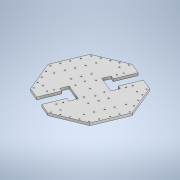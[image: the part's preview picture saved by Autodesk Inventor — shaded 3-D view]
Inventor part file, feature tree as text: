
AUTODESK INVENTOR PART (.ipt)
format: ipt  version: 2020 (Build 240168000, 168)  size: 396,288 bytes
history: native  units: mm
features: extrude x2, sketch x2
ambient origin geometry x8: Origin, YZ Plane, XZ Plane, XY Plane, X Axis, Y Axis, Z Axis, Center Point
bodies: Solide1 (feature_tree)
feature tree (4):
  extrude  "Extrusion1"  Depth=10.0mm TaperAngle=0.0deg
  extrude  "Extrusion2"  Depth=4.5mm
  sketch  "Esquisse1"
  sketch  "Esquisse2"
